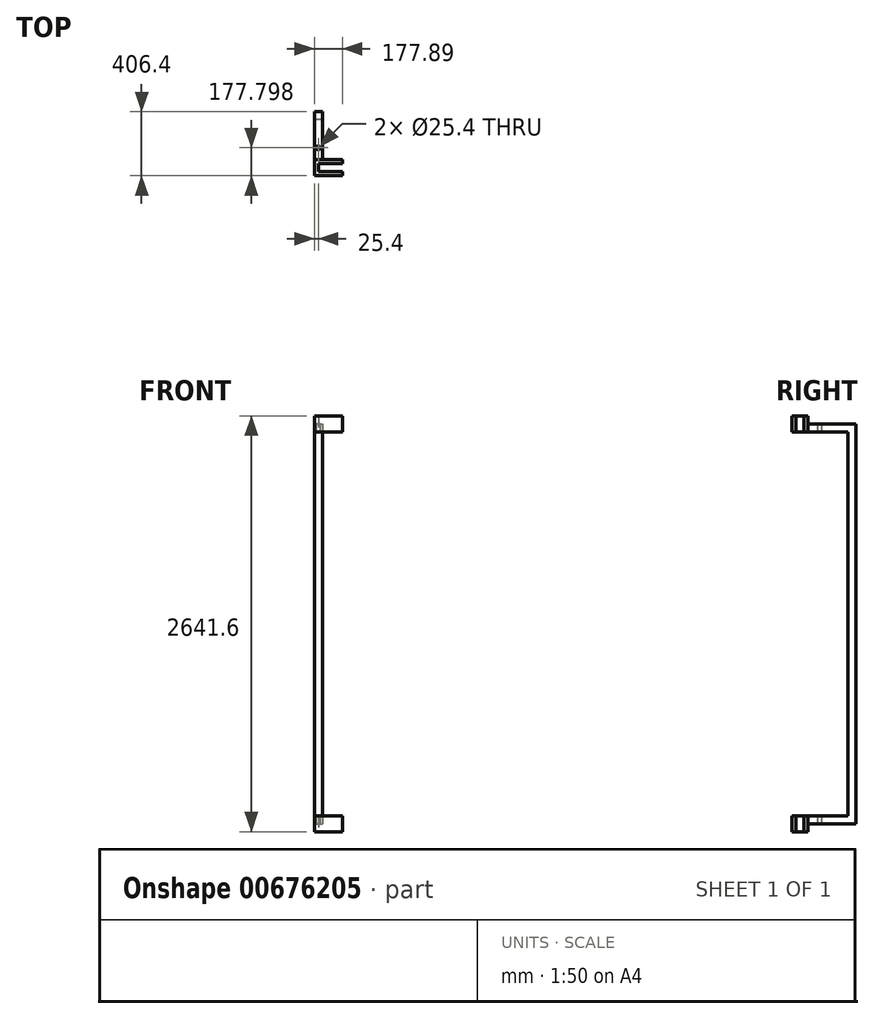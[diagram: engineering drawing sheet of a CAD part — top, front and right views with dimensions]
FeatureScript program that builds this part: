
annotation { "Feature Type Name" : "Feature", "Feature Type Description" : "" }
export const myFeature = defineFeature(function(context is Context, id is Id, definition is map)
    precondition{}
    {
        {
            var Q0;
            Q0=qCreatedBy(makeId("Top.planeOp"),FACE);
            var sketch = newSketch(context, id + "F0", { "sketchPlane" : qUnion([Q0])});
            skLineSegment(sketch, "E0.bottom", {"start": v(-99.37, 10.38) * mm, "end": v(78.43, 10.38) * mm});
            skLineSegment(sketch, "E0.top", {"start": v(-99.37, -15.02) * mm, "end": v(78.43, -15.02) * mm});
            skLineSegment(sketch, "E0.left", {"start": v(-99.37, 10.38) * mm, "end": v(-99.37, -15.02) * mm});
            skLineSegment(sketch, "E0.right", {"start": v(78.43, 10.38) * mm, "end": v(78.43, -15.02) * mm});
            skLineSegment(sketch, "E1.bottom", {"start": v(-99.37, -15.02) * mm, "end": v(-73.97, -15.02) * mm});
            skLineSegment(sketch, "E1.top", {"start": v(-99.37, 86.58) * mm, "end": v(-73.97, 86.58) * mm});
            skLineSegment(sketch, "E1.left", {"start": v(-99.37, -15.02) * mm, "end": v(-99.37, 86.58) * mm});
            skLineSegment(sketch, "E1.right", {"start": v(-73.97, -15.02) * mm, "end": v(-73.97, 86.58) * mm});
            skLineSegment(sketch, "E2.bottom", {"start": v(-99.37, 86.58) * mm, "end": v(78.43, 86.58) * mm});
            skLineSegment(sketch, "E2.top", {"start": v(-99.37, 61.18) * mm, "end": v(78.43, 61.18) * mm});
            skLineSegment(sketch, "E2.left", {"start": v(-99.37, 86.58) * mm, "end": v(-99.37, 61.18) * mm});
            skLineSegment(sketch, "E2.right", {"start": v(78.43, 86.58) * mm, "end": v(78.43, 61.18) * mm});
            skSolve(sketch);
        }
        {
            var Q0;
            Q0 = qSketchRegion(id + "F0", true);
            extrude(context, id + "F1", {"entities" : qUnion([Q0]), "depth" : 101.6 * mm, "offsetDistance" : 25 * mm});
        }
        {
            var Q0;
            Q0=makeQuery(id+"F1.opExtrude","SWEPT_FACE",FACE,{"disambiguationData":[OSD([sQuery(id+"F0.wireOp",EDGE,"E2.bottom")])]});
            var sketch = newSketch(context, id + "F2", { "sketchPlane" : qUnion([Q0])});
            skLineSegment(sketch, "E3.bottom", {"start": v(99.37, 101.6) * mm, "end": v(48.57, 101.6) * mm});
            skLineSegment(sketch, "E3.top", {"start": v(99.37, 50.8) * mm, "end": v(48.57, 50.8) * mm});
            skLineSegment(sketch, "E3.left", {"start": v(99.37, 101.6) * mm, "end": v(99.37, 50.8) * mm});
            skLineSegment(sketch, "E3.right", {"start": v(48.57, 101.6) * mm, "end": v(48.57, 50.8) * mm});
            skSolve(sketch);
        }
        {
            var Q0;
            Q0 = qSketchRegion(id + "F2", true);
            extrude(context, id + "F3", {"entities" : qUnion([Q0]), "operationType" : NewBodyOperationType.ADD, "depth" : 304.8 * mm, "offsetDistance" : 25 * mm});
        }
        {
            var Q0;
            Q0=makeQuery(id+"F3.boolean.opBoolean","MERGE",FACE,{"derivedFrom":[makeQuery(id+"F1.opExtrude","CAP_FACE",FACE,{"disambiguationData":[OSD([sQuery(id+"F0.wireOp",EDGE,"E0.bottom"),sQuery(id+"F0.wireOp",EDGE,"E0.top"),sQuery(id+"F0.wireOp",EDGE,"E0.right"),sQuery(id+"F0.wireOp",EDGE,"E1.bottom"),sQuery(id+"F0.wireOp",EDGE,"E1.left"),sQuery(id+"F0.wireOp",EDGE,"E1.right"),sQuery(id+"F0.wireOp",EDGE,"E2.bottom"),sQuery(id+"F0.wireOp",EDGE,"E2.top"),sQuery(id+"F0.wireOp",EDGE,"E2.left"),sQuery(id+"F0.wireOp",EDGE,"E2.right")])],"isStart":false}),makeQuery(id+"F3.opExtrude","SWEPT_FACE",FACE,{"disambiguationData":[OSD([sQuery(id+"F2.wireOp",EDGE,"E3.bottom")])]})]});
            var sketch = newSketch(context, id + "F4", { "sketchPlane" : qUnion([Q0])});
            skLineSegment(sketch, "E4.bottom", {"start": v(-48.57, 391.38) * mm, "end": v(-99.37, 391.38) * mm});
            skLineSegment(sketch, "E4.top", {"start": v(-48.57, 340.58) * mm, "end": v(-99.37, 340.58) * mm});
            skLineSegment(sketch, "E4.left", {"start": v(-48.57, 391.38) * mm, "end": v(-48.57, 340.58) * mm});
            skLineSegment(sketch, "E4.right", {"start": v(-99.37, 391.38) * mm, "end": v(-99.37, 340.58) * mm});
            skSolve(sketch);
        }
        {
            var Q0;
            Q0 = qSketchRegion(id + "F4", true);
            extrude(context, id + "F5", {"entities" : qUnion([Q0]), "operationType" : NewBodyOperationType.ADD, "depth" : 2489.2 * mm, "offsetDistance" : 25 * mm});
        }
        {
            var Q0;
            Q0=makeQuery(id+"F5.opExtrude","SWEPT_FACE",FACE,{"disambiguationData":[OSD([sQuery(id+"F4.wireOp",EDGE,"E4.top")])]});
            var sketch = newSketch(context, id + "F6", { "sketchPlane" : qUnion([Q0])});
            skLineSegment(sketch, "E5.bottom", {"start": v(-99.37, 2590.8) * mm, "end": v(-48.57, 2590.8) * mm});
            skLineSegment(sketch, "E5.top", {"start": v(-99.37, 2540) * mm, "end": v(-48.57, 2540) * mm});
            skLineSegment(sketch, "E5.left", {"start": v(-99.37, 2590.8) * mm, "end": v(-99.37, 2540) * mm});
            skLineSegment(sketch, "E5.right", {"start": v(-48.57, 2590.8) * mm, "end": v(-48.57, 2540) * mm});
            skSolve(sketch);
        }
        {
            var Q0;
            Q0 = qSketchRegion(id + "F6", true);
            extrude(context, id + "F7", {"entities" : qUnion([Q0]), "operationType" : NewBodyOperationType.ADD, "depth" : 254 * mm, "offsetDistance" : 25 * mm});
        }
        {
            var Q0;
            Q0=makeQuery(id+"F7.opExtrude","SWEPT_FACE",FACE,{"disambiguationData":[OSD([sQuery(id+"F6.wireOp",EDGE,"E5.top")])]});
            var sketch = newSketch(context, id + "F8", { "sketchPlane" : qUnion([Q0])});
            skLineSegment(sketch, "E6.bottom", {"start": v(-99.37, -86.58) * mm, "end": v(78.43, -86.58) * mm});
            skLineSegment(sketch, "E6.top", {"start": v(-99.37, -61.18) * mm, "end": v(78.43, -61.18) * mm});
            skLineSegment(sketch, "E6.left", {"start": v(-99.37, -86.58) * mm, "end": v(-99.37, -61.18) * mm});
            skLineSegment(sketch, "E6.right", {"start": v(78.43, -86.58) * mm, "end": v(78.43, -61.18) * mm});
            skLineSegment(sketch, "E7.bottom", {"start": v(-99.37, -61.18) * mm, "end": v(-73.97, -61.18) * mm});
            skLineSegment(sketch, "E7.top", {"start": v(-99.37, 15.02) * mm, "end": v(-73.97, 15.02) * mm});
            skLineSegment(sketch, "E7.left", {"start": v(-99.37, -61.18) * mm, "end": v(-99.37, 15.02) * mm});
            skLineSegment(sketch, "E7.right", {"start": v(-73.97, -61.18) * mm, "end": v(-73.97, 15.02) * mm});
            skLineSegment(sketch, "E8.bottom", {"start": v(-73.97, 15.02) * mm, "end": v(78.52, 15.02) * mm});
            skLineSegment(sketch, "E8.top", {"start": v(-73.97, -10.38) * mm, "end": v(78.52, -10.38) * mm});
            skLineSegment(sketch, "E8.left", {"start": v(-73.97, 15.02) * mm, "end": v(-73.97, -10.38) * mm});
            skLineSegment(sketch, "E8.right", {"start": v(78.52, 15.02) * mm, "end": v(78.52, -10.38) * mm});
            skSolve(sketch);
        }
        {
            var Q0;
            Q0 = qSketchRegion(id + "F8", true);
            extrude(context, id + "F9", {"entities" : qUnion([Q0]), "operationType" : NewBodyOperationType.ADD, "oppositeDirection" : true, "depth" : 101.6 * mm, "offsetDistance" : 25 * mm});
        }
        {
            var Q0;
            Q0=makeQuery(id+"F7.boolean.opBoolean","MERGE",FACE,{"derivedFrom":[makeQuery(id+"F5.opExtrude","CAP_FACE",FACE,{"disambiguationData":[OSD([sQuery(id+"F4.wireOp",EDGE,"E4.bottom"),sQuery(id+"F4.wireOp",EDGE,"E4.top"),sQuery(id+"F4.wireOp",EDGE,"E4.left"),sQuery(id+"F4.wireOp",EDGE,"E4.right")])],"isStart":false}),makeQuery(id+"F7.opExtrude","SWEPT_FACE",FACE,{"disambiguationData":[OSD([sQuery(id+"F6.wireOp",EDGE,"E5.bottom")])]})]});
            var sketch = newSketch(context, id + "F10", { "sketchPlane" : qUnion([Q0])});
            skPoint(sketch, "E9", {"position": v(-73.97, 162.78) * mm});
            skSolve(sketch);
        }
        {
            var Q0;
            Q0=sQuery(id+"F10.wireOp",VERTEX,"E9");
            var Q1;
            Q1=makeQuery(id+"F1.opExtrude","SWEPT_BODY",BODY,{"disambiguationData":[OSD([sQuery(id+"F0.wireOp",EDGE,"E0.bottom"),sQuery(id+"F0.wireOp",EDGE,"E0.top"),sQuery(id+"F0.wireOp",EDGE,"E0.right"),sQuery(id+"F0.wireOp",EDGE,"E1.bottom"),sQuery(id+"F0.wireOp",EDGE,"E1.left"),sQuery(id+"F0.wireOp",EDGE,"E1.right"),sQuery(id+"F0.wireOp",EDGE,"E2.bottom"),sQuery(id+"F0.wireOp",EDGE,"E2.top"),sQuery(id+"F0.wireOp",EDGE,"E2.left"),sQuery(id+"F0.wireOp",EDGE,"E2.right")])]});
            hole(context, id + "F11", {"style" : HoleStyle.SIMPLE, "endStyle" : HoleEndStyle.BLIND, "holeDiameter" : 25.4 * mm, "majorDiameter" : 5 * mm, "holeDepth" : 2540 * mm, "isTappedThrough" : true, "tappedDepth" : 12 * mm, "tapClearance" : 3, "locations" : qUnion([Q0]), "scope" : qUnion([Q1])});
        }
    });
